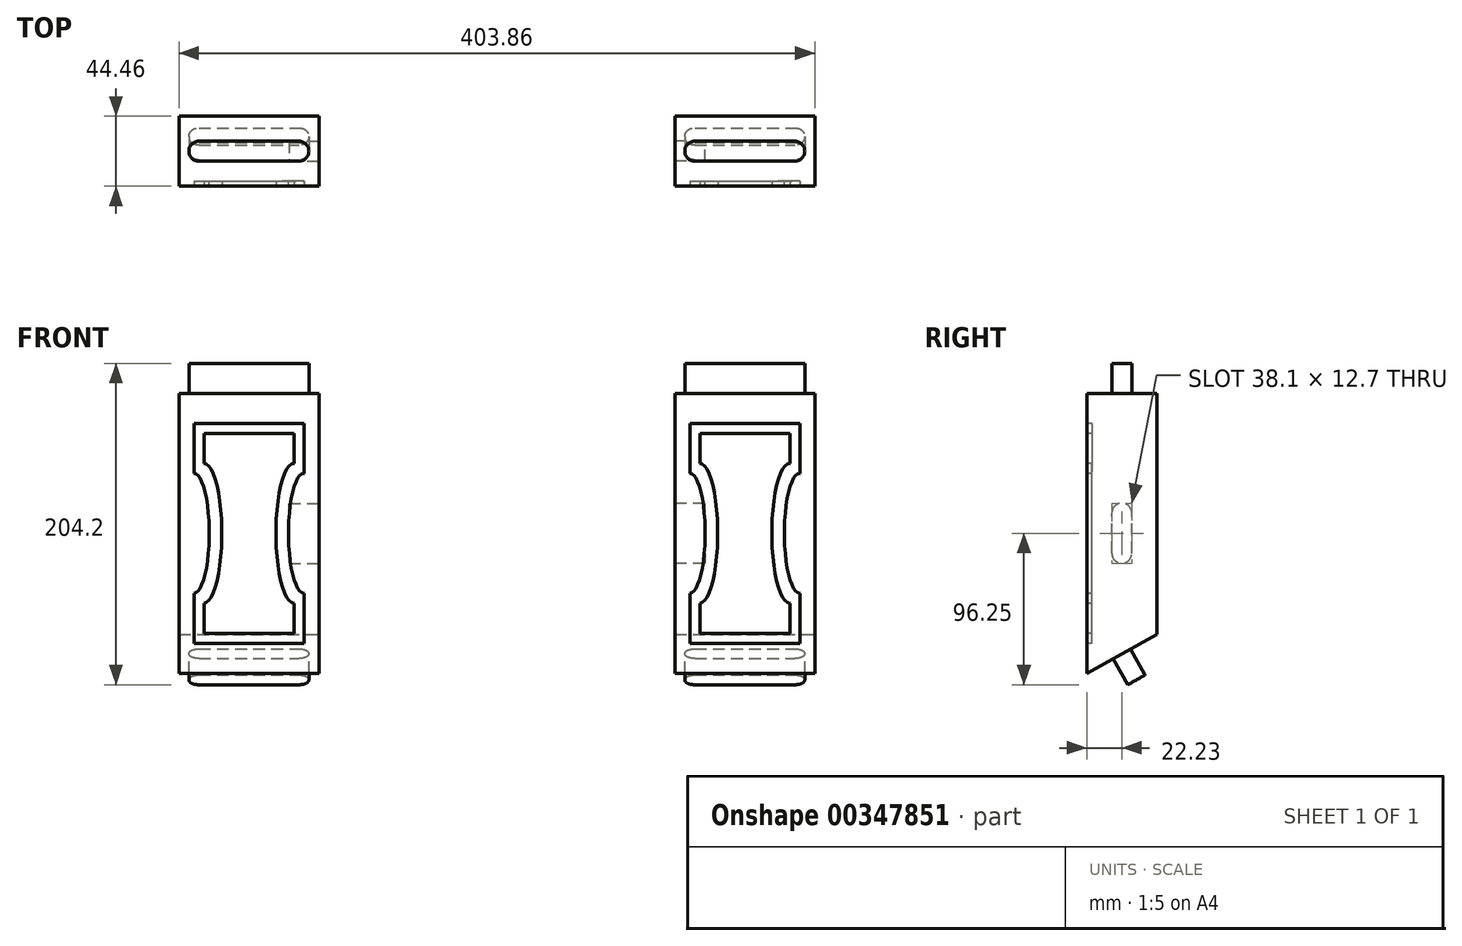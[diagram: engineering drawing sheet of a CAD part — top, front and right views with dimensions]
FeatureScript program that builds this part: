
annotation { "Feature Type Name" : "Feature", "Feature Type Description" : "" }
export const myFeature = defineFeature(function(context is Context, id is Id, definition is map)
    precondition{}
    {
        {
            var Q0;
            Q0=qCreatedBy(makeId("Front.planeOp"),FACE);
            var sketch = newSketch(context, id + "F0", { "sketchPlane" : qUnion([Q0])});
            skLineSegment(sketch, "E0.bottom", {"start": v(44.45, 88.9) * mm, "end": v(-44.45, 88.9) * mm});
            skLineSegment(sketch, "E0.top", {"start": v(44.45, -88.9) * mm, "end": v(-44.45, -88.9) * mm});
            skLineSegment(sketch, "E0.left", {"start": v(44.45, 88.9) * mm, "end": v(44.45, -88.9) * mm});
            skLineSegment(sketch, "E0.right", {"start": v(-44.45, 88.9) * mm, "end": v(-44.45, -88.9) * mm});
            skPoint(sketch, "E0.middle", {"position": v(0, 0) * mm});
            skSolve(sketch);
        }
        {
            var Q0;
            Q0=makeQuery(id+"F0.imprint","IMPRINT",FACE,{"disambiguationData":[TD([[makeQuery(id+"F0.imprint","IMPRINT",EDGE,{"derivedFrom":sQuery(id+"F0.wireOp",EDGE,"E0.bottom")}),1.0]])]});
            extrude(context, id + "F1", {"entities" : qUnion([Q0]), "endBound" : BoundingType.SYMMETRIC, "depth" : 44.45 * mm});
        }
        {
            var Q0;
            Q0=makeQuery(id+"F1.opExtrude","SWEPT_FACE",FACE,{"disambiguationData":[OSD([sQuery(id+"F0.wireOp",EDGE,"E0.bottom")])]});
            var sketch = newSketch(context, id + "F2", { "sketchPlane" : qUnion([Q0])});
            skLineSegment(sketch, "E1", {"start": v(-54.52, 0) * mm, "end": v(52.1, 0) * mm, "construction": true});
            skPoint(sketch, "E1.startSnap0", {"position": v(-44.45, 0) * mm});
            skLineSegment(sketch, "E2", {"start": v(0, 29.72) * mm, "end": v(0, -27.63) * mm, "construction": true});
            skPoint(sketch, "E2.startSnap0", {"position": v(0, 22.23) * mm});
            skPoint(sketch, "E2.endSnap0", {"position": v(0, -22.23) * mm});
            skLineSegment(sketch, "E3.bottom", {"start": v(-31.75, 6.35) * mm, "end": v(31.75, 6.35) * mm});
            skLineSegment(sketch, "E3.top", {"start": v(-31.75, -6.35) * mm, "end": v(31.75, -6.35) * mm});
            skLineSegment(sketch, "E3.left", {"start": v(-31.75, 6.35) * mm, "end": v(-31.75, -6.35) * mm, "construction": true});
            skLineSegment(sketch, "E3.right", {"start": v(31.75, 6.35) * mm, "end": v(31.75, -6.35) * mm, "construction": true});
            skPoint(sketch, "E3.middle", {"position": v(0, 0) * mm});
            skArc(sketch, "E4", {"start": v(-31.75, 6.35) * mm, "mid": v(-38.1, 0) * mm, "end": v(-31.75, -6.35) * mm});
            skArc(sketch, "E5", {"start": v(31.75, -6.35) * mm, "mid": v(38.1, 0) * mm, "end": v(31.75, 6.35) * mm});
            skSolve(sketch);
        }
        {
            var Q0;
            Q0=makeQuery(id+"F2.imprint","IMPRINT",FACE,{"disambiguationData":[TD([[makeQuery(id+"F2.imprint","IMPRINT",EDGE,{"derivedFrom":sQuery(id+"F2.wireOp",EDGE,"E3.bottom")}),-1.0]])]});
            extrude(context, id + "F3", {"entities" : qUnion([Q0]), "operationType" : NewBodyOperationType.ADD, "depth" : 19.05 * mm});
        }
        {
            var Q0;
            Q0=makeQuery(id+"F1.opExtrude","CAP_FACE",FACE,{"disambiguationData":[OSD([sQuery(id+"F0.wireOp",EDGE,"E0.bottom"),sQuery(id+"F0.wireOp",EDGE,"E0.top"),sQuery(id+"F0.wireOp",EDGE,"E0.left"),sQuery(id+"F0.wireOp",EDGE,"E0.right")])],"isStart":false});
            var sketch = newSketch(context, id + "F4", { "sketchPlane" : qUnion([Q0])});
            skLineSegment(sketch, "E6", {"start": v(0, 88.9) * mm, "end": v(0, -88.9) * mm, "construction": true});
            skLineSegment(sketch, "E7", {"start": v(-44.45, 0) * mm, "end": v(44.45, 0) * mm, "construction": true});
            skLineSegment(sketch, "E8.bottom", {"start": v(-34.93, 69.85) * mm, "end": v(34.92, 69.85) * mm});
            skPoint(sketch, "E8.middle", {"position": v(0, 0) * mm});
            skLineSegment(sketch, "E9.0", {"start": v(-28.58, 63.5) * mm, "end": v(28.58, 63.5) * mm});
            skLineSegment(sketch, "E10", {"start": v(-28.58, 63.5) * mm, "end": v(-28.58, 44.45) * mm});
            skLineSegment(sketch, "E11.MirrorCS", {"start": v(-28.58, -63.5) * mm, "end": v(-28.58, -44.45) * mm});
            skLineSegment(sketch, "E12.MirrorCS", {"start": v(28.57, 63.5) * mm, "end": v(28.57, 44.45) * mm});
            skLineSegment(sketch, "E13.MirrorCS", {"start": v(28.58, -63.5) * mm, "end": v(28.58, -44.45) * mm});
            skLineSegment(sketch, "E14", {"start": v(-34.93, 69.85) * mm, "end": v(-34.93, 38.1) * mm});
            skLineSegment(sketch, "E15.MirrorCS", {"start": v(34.92, 69.85) * mm, "end": v(34.92, 38.1) * mm});
            skLineSegment(sketch, "E16.MirrorCS", {"start": v(-34.93, -69.85) * mm, "end": v(-34.93, -38.1) * mm});
            skLineSegment(sketch, "E17.MirrorCS", {"start": v(34.92, -69.85) * mm, "end": v(34.92, -38.1) * mm});
            skPoint(sketch, "E18.orphan", {"position": v(-34.93, -69.85) * mm});
            skPoint(sketch, "E8.top.end.orphan", {"position": v(34.92, -69.85) * mm});
            skLineSegment(sketch, "E19.MirrorCS", {"start": v(-28.58, -63.5) * mm, "end": v(28.58, -63.5) * mm});
            skLineSegment(sketch, "E20.MirrorCS", {"start": v(-34.93, -69.85) * mm, "end": v(34.93, -69.85) * mm});
            skLineSegment(sketch, "E21", {"start": v(-34.93, 38.1) * mm, "end": v(-34.93, -38.1) * mm, "construction": true});
            skLineSegment(sketch, "E22", {"start": v(-28.58, 44.45) * mm, "end": v(-28.58, -44.45) * mm, "construction": true});
            skEllipticalArc(sketch, "E23", {});
            skEllipticalArc(sketch, "E24", {});
            skEllipticalArc(sketch, "E25.trimOffspring", {});
            skEllipticalArc(sketch, "E26.trimOffspring", {});
            skEllipticalArc(sketch, "E27.MirrorCS", {});
            skEllipticalArc(sketch, "E28.MirrorCS", {});
            const initialGuessF4  = {"E23": [-0.034925, 0, 0, 1, 0.0381, 0.009747932984064105, 3.141592653589793, 0], "E24": [-0.028575, 0, 0, 1, 0.04445, 0.011425213810996485, 2.5522817580940105, 2.5987378353244415], "E25.trimOffspring": [-0.028575, 0, 0, 1, 0.04445, 0.011425213810996485, 0.5428548182653515, 0.589310895495783], "E26.trimOffspring": [-0.028575, 0, 0, 1, 0.04445, 0.011425213810996485, 3.141592653589793, 0], "E27.MirrorCS": [0.028575, 0, 0, 1, 0.04445, 0.011425213810996485, 0, 3.141592653589793], "E28.MirrorCS": [0.034925, 0, 0, 1, 0.0381, 0.009747932984064105, 0, 3.141592653589793]};
            skSetInitialGuess(sketch, initialGuessF4);
            skSolve(sketch);
        }
        {
            var Q0;
            Q0=makeQuery(id+"F4.imprint","IMPRINT",FACE,{"disambiguationData":[TD([[makeQuery(id+"F4.imprint","IMPRINT",EDGE,{"derivedFrom":sQuery(id+"F4.wireOp",EDGE,"E8.bottom")}),-1.0]])]});
            extrude(context, id + "F5", {"entities" : qUnion([Q0]), "operationType" : NewBodyOperationType.REMOVE, "oppositeDirection" : true, "depth" : 3.17 * mm});
        }
        {
            var Q0;
            Q0=makeQuery(id+"F1.opExtrude","SWEPT_FACE",FACE,{"disambiguationData":[OSD([sQuery(id+"F0.wireOp",EDGE,"E0.left")])]});
            var sketch = newSketch(context, id + "F6", { "sketchPlane" : qUnion([Q0])});
            skLineSegment(sketch, "E29", {"start": v(-22.23, -88.9) * mm, "end": v(22.23, -64.14) * mm});
            skSolve(sketch);
        }
        {
            var Q0;
            {var subQ0=sQuery(id+"F6.wireOp",EDGE,"E29");Q0=makeQuery(id+"F6.imprint","IMPRINT",FACE,{"disambiguationData":[TD([[makeQuery(id+"F6.imprint","IMPRINT",EDGE,{"derivedFrom":subQ0}),-1.0]])]});}
            extrude(context, id + "F7", {"entities" : qUnion([Q0]), "operationType" : NewBodyOperationType.REMOVE, "oppositeDirection" : true, "depth" : 88.9 * mm});
        }
        {
            var Q0;
            Q0=makeQuery(id+"F7.boolean.opBoolean","COPY",FACE,{"derivedFrom":makeQuery(id+"F7.opExtrude","SWEPT_FACE",FACE,{"disambiguationData":[OSD([sQuery(id+"F6.wireOp",EDGE,"E29")])]})});
            var sketch = newSketch(context, id + "F8", { "sketchPlane" : qUnion([Q0])});
            skLineSegment(sketch, "E30", {"start": v(-48.25, 37.23) * mm, "end": v(49.71, 37.23) * mm, "construction": true});
            skPoint(sketch, "E30.startSnap0", {"position": v(-44.45, 37.23) * mm});
            skLineSegment(sketch, "E31", {"start": v(0, 63) * mm, "end": v(0, 4.22) * mm, "construction": true});
            skPoint(sketch, "E31.startSnap0", {"position": v(0, 62.67) * mm});
            skPoint(sketch, "E31.endSnap0", {"position": v(0, 11.8) * mm});
            skLineSegment(sketch, "E32.bottom", {"start": v(-31.75, 30.88) * mm, "end": v(31.75, 30.88) * mm});
            skLineSegment(sketch, "E32.top", {"start": v(-31.75, 43.58) * mm, "end": v(31.75, 43.58) * mm});
            skPoint(sketch, "E32.middle", {"position": v(0, 37.23) * mm});
            skArc(sketch, "E33", {"start": v(-31.75, 43.58) * mm, "mid": v(-38.1, 37.23) * mm, "end": v(-31.75, 30.88) * mm});
            skArc(sketch, "E34", {"start": v(31.75, 30.88) * mm, "mid": v(38.1, 37.23) * mm, "end": v(31.75, 43.58) * mm});
            skSolve(sketch);
        }
        {
            var Q0;
            Q0=makeQuery(id+"F8.imprint","IMPRINT",FACE,{"disambiguationData":[TD([[makeQuery(id+"F8.imprint","IMPRINT",EDGE,{"derivedFrom":sQuery(id+"F8.wireOp",EDGE,"E32.bottom")}),1.0]])]});
            extrude(context, id + "F9", {"entities" : qUnion([Q0]), "operationType" : NewBodyOperationType.ADD, "depth" : 19.05 * mm});
        }
        {
            var Q0;
            Q0=makeQuery(id+"F1.opExtrude","SWEPT_BODY",BODY,{"disambiguationData":[OSD([sQuery(id+"F0.wireOp",EDGE,"E0.bottom"),sQuery(id+"F0.wireOp",EDGE,"E0.top"),sQuery(id+"F0.wireOp",EDGE,"E0.left"),sQuery(id+"F0.wireOp",EDGE,"E0.right")])]});
            transform(context, id + "F10", {"entities" : qUnion([Q0]), "transformType" : TransformType.TRANSLATION_3D, "dx" : -314.96 * mm, "dy" : 0 * mm, "dz" : 0 * mm, "makeCopy" : true});
        }
        {
            var Q0;
            Q0=makeQuery(id+"F1.opExtrude","SWEPT_FACE",FACE,{"disambiguationData":[OSD([sQuery(id+"F0.wireOp",EDGE,"E0.right")])]});
            var sketch = newSketch(context, id + "F11", { "sketchPlane" : qUnion([Q0])});
            skLineSegment(sketch, "E35", {"start": v(0, 88.9) * mm, "end": v(0, -76.52) * mm, "construction": true});
            skLineSegment(sketch, "E36", {"start": v(22.23, 0) * mm, "end": v(-22.23, 0) * mm, "construction": true});
            skLineSegment(sketch, "E37", {"start": v(0, 77.97) * mm, "end": v(0, -76.52) * mm, "construction": true});
            skLineSegment(sketch, "E38.left", {"start": v(6.35, -12.7) * mm, "end": v(6.35, 12.7) * mm});
            skLineSegment(sketch, "E38.right", {"start": v(-6.35, -12.7) * mm, "end": v(-6.35, 12.7) * mm});
            skPoint(sketch, "E38.middle", {"position": v(0, 0) * mm});
            skArc(sketch, "E39", {"start": v(6.35, 12.7) * mm, "mid": v(0, 19.05) * mm, "end": v(-6.35, 12.7) * mm});
            skArc(sketch, "E40", {"start": v(-6.35, -12.7) * mm, "mid": v(0, -19.05) * mm, "end": v(6.35, -12.7) * mm});
            skSolve(sketch);
        }
        {
            var Q0;
            Q0=makeQuery(id+"F11.imprint","IMPRINT",FACE,{"disambiguationData":[TD([[makeQuery(id+"F11.imprint","IMPRINT",EDGE,{"derivedFrom":sQuery(id+"F11.wireOp",EDGE,"E38.left")}),1.0]])]});
            extrude(context, id + "F12", {"entities" : qUnion([Q0]), "operationType" : NewBodyOperationType.REMOVE, "oppositeDirection" : true, "depth" : 19.05 * mm});
        }
        {
            var Q0;
            Q0=makeQuery(id+"F10.opPattern","COPY",FACE,{"derivedFrom":makeQuery(id+"F1.opExtrude","SWEPT_FACE",FACE,{"disambiguationData":[OSD([sQuery(id+"F0.wireOp",EDGE,"E0.left")])]}),"instanceName":"1"});
            var sketch = newSketch(context, id + "F13", { "sketchPlane" : qUnion([Q0])});
            skLineSegment(sketch, "E41", {"start": v(0, 88.9) * mm, "end": v(0, -83.52) * mm, "construction": true});
            skPoint(sketch, "E41.endSnap0", {"position": v(0, -76.52) * mm});
            skLineSegment(sketch, "E42", {"start": v(-22.23, 0) * mm, "end": v(22.23, 0) * mm, "construction": true});
            skLineSegment(sketch, "E43", {"start": v(0, 83.44) * mm, "end": v(0, -71.06) * mm, "construction": true});
            skLineSegment(sketch, "E44", {"start": v(22.22, 0) * mm, "end": v(-22.23, 0) * mm, "construction": true});
            skLineSegment(sketch, "E45.left", {"start": v(6.35, -12.7) * mm, "end": v(6.35, 12.7) * mm});
            skLineSegment(sketch, "E45.right", {"start": v(-6.35, -12.7) * mm, "end": v(-6.35, 12.7) * mm});
            skPoint(sketch, "E45.middle", {"position": v(0, 0) * mm});
            skArc(sketch, "E46", {"start": v(6.35, 12.7) * mm, "mid": v(0, 19.05) * mm, "end": v(-6.35, 12.7) * mm});
            skArc(sketch, "E47", {"start": v(-6.35, -12.7) * mm, "mid": v(0, -19.05) * mm, "end": v(6.35, -12.7) * mm});
            skSolve(sketch);
        }
        {
            var Q0;
            Q0=makeQuery(id+"F13.imprint","IMPRINT",FACE,{"disambiguationData":[TD([[makeQuery(id+"F13.imprint","IMPRINT",EDGE,{"derivedFrom":sQuery(id+"F13.wireOp",EDGE,"E45.left")}),1.0]])]});
            extrude(context, id + "F14", {"entities" : qUnion([Q0]), "operationType" : NewBodyOperationType.REMOVE, "oppositeDirection" : true, "depth" : 19.05 * mm});
        }
    });
